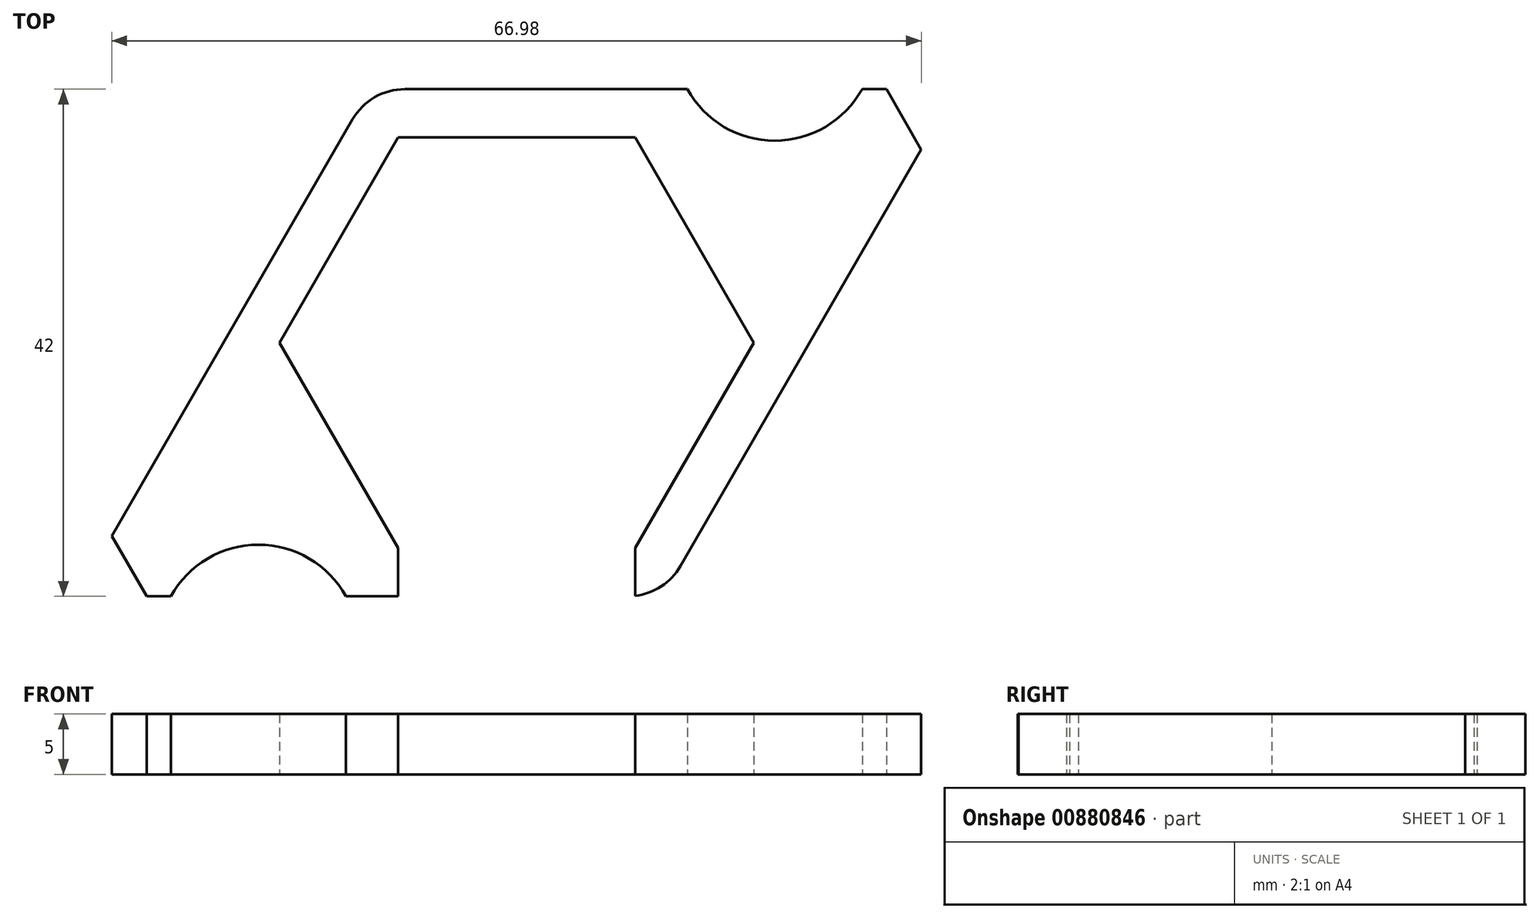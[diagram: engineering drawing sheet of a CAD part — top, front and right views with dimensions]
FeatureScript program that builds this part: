
annotation { "Feature Type Name" : "Feature", "Feature Type Description" : "" }
export const myFeature = defineFeature(function(context is Context, id is Id, definition is map)
    precondition{}
    {
        {
            var Q0;
            Q0=qCreatedBy(makeId("Top.planeOp"),FACE);
            var sketch = newSketch(context, id + "F0", { "sketchPlane" : qUnion([Q0])});
            skCircle(sketch, "E0.cCircle", {"center": v(0, 0) * mm, "radius": 17 * mm, "construction": true});
            skLineSegment(sketch, "E0.0", {"start": v(-19.63, 0) * mm, "end": v(-9.81, 17) * mm});
            skLineSegment(sketch, "E0.1", {"start": v(-9.81, 17) * mm, "end": v(9.81, 17) * mm});
            skLineSegment(sketch, "E0.2", {"start": v(9.81, 17) * mm, "end": v(19.63, 0) * mm});
            skLineSegment(sketch, "E0.3", {"start": v(19.63, 0) * mm, "end": v(9.81, -17) * mm});
            skLineSegment(sketch, "E0.4", {"start": v(9.81, -17) * mm, "end": v(-9.81, -17) * mm});
            skLineSegment(sketch, "E0.5", {"start": v(-9.81, -17) * mm, "end": v(-19.63, 0) * mm});
            skPoint(sketch, "E0.0.midPoint", {"position": v(-14.72, 8.5) * mm});
            skLineSegment(sketch, "E1.0", {"start": v(-24.25, 0) * mm, "end": v(-13.57, 18.5) * mm});
            skLineSegment(sketch, "E1.1", {"start": v(12.12, 21) * mm, "end": v(24.25, 0) * mm});
            skLineSegment(sketch, "E1.2", {"start": v(24.25, 0) * mm, "end": v(13.57, -18.5) * mm});
            skLineSegment(sketch, "E1.3", {"start": v(-9.24, 21) * mm, "end": v(12.12, 21) * mm});
            skLineSegment(sketch, "E1.4", {"start": v(9.24, -21) * mm, "end": v(-12.12, -21) * mm});
            skLineSegment(sketch, "E1.5", {"start": v(-12.12, -21) * mm, "end": v(-24.25, 0) * mm});
            skLineSegment(sketch, "E2", {"start": v(-24.25, 0) * mm, "end": v(-33.49, -16) * mm});
            skLineSegment(sketch, "E3", {"start": v(-33.49, -16) * mm, "end": v(-30.6, -21) * mm});
            skLineSegment(sketch, "E4", {"start": v(-30.6, -21) * mm, "end": v(-12.12, -21) * mm});
            skLineSegment(sketch, "E5", {"start": v(-9.81, 17) * mm, "end": v(9.81, -17) * mm, "construction": true});
            skLineSegment(sketch, "E6.MirrorCS", {"start": v(12.12, 21) * mm, "end": v(30.6, 21) * mm});
            skLineSegment(sketch, "E7.MirrorCS", {"start": v(30.6, 21) * mm, "end": v(33.49, 16) * mm});
            skLineSegment(sketch, "E8.MirrorCS", {"start": v(33.49, 16) * mm, "end": v(24.25, 0) * mm});
            skPoint(sketch, "E9", {"position": v(0, -21) * mm});
            skLineSegment(sketch, "E10", {"start": v(-3, -21) * mm, "end": v(-3, -17) * mm});
            skLineSegment(sketch, "E11.MirrorCS", {"start": v(3, -21) * mm, "end": v(3, -17) * mm});
            skArc(sketch, "E12", {"start": v(-14.12, -21) * mm, "mid": v(-21.36, -16.73) * mm, "end": v(-28.6, -21) * mm});
            skArc(sketch, "E13", {"start": v(14.12, 21) * mm, "mid": v(21.36, 16.73) * mm, "end": v(28.6, 21) * mm});
            skLineSegment(sketch, "E14", {"start": v(-9.81, -17) * mm, "end": v(-9.81, -21) * mm});
            skLineSegment(sketch, "E15", {"start": v(9.81, -17) * mm, "end": v(9.81, -21) * mm});
            skPoint(sketch, "E16.visualSharp", {"position": v(-12.12, 21) * mm});
            skArc(sketch, "E16.filletArc", {"start": v(-9.24, 21) * mm, "mid": v(-11.74, 20.33) * mm, "end": v(-13.57, 18.5) * mm});
            skPoint(sketch, "E17.visualSharp", {"position": v(12.12, -21) * mm});
            skArc(sketch, "E17.filletArc", {"start": v(9.24, -21) * mm, "mid": v(11.74, -20.33) * mm, "end": v(13.57, -18.5) * mm});
            skSolve(sketch);
        }
        {
            var Q0;
            {var subQ3=sQuery(id+"F0.wireOp",EDGE,"E1.1");Q0=makeQuery(id+"F0.imprint","IMPRINT",FACE,{"disambiguationData":[TD([[makeQuery(id+"F0.imprint","IMPRINT",EDGE,{"derivedFrom":subQ3}),1.0]])]});}
            var Q1;
            Q1=makeQuery(id+"F0.imprint","IMPRINT",FACE,{"disambiguationData":[TD([[makeQuery(id+"F0.imprint","IMPRINT",EDGE,{"derivedFrom":sQuery(id+"F0.wireOp",EDGE,"E0.0")}),1.0]])]});
            var Q2;
            {var subQ3=sQuery(id+"F0.wireOp",EDGE,"E1.5");Q2=makeQuery(id+"F0.imprint","IMPRINT",FACE,{"disambiguationData":[TD([[makeQuery(id+"F0.imprint","IMPRINT",EDGE,{"derivedFrom":subQ3}),1.0]])]});}
            extrude(context, id + "F1", {"entities" : qUnion([Q0, Q1, Q2]), "depth" : 5 * mm, "offsetDistance" : 25 * mm});
        }
    });
